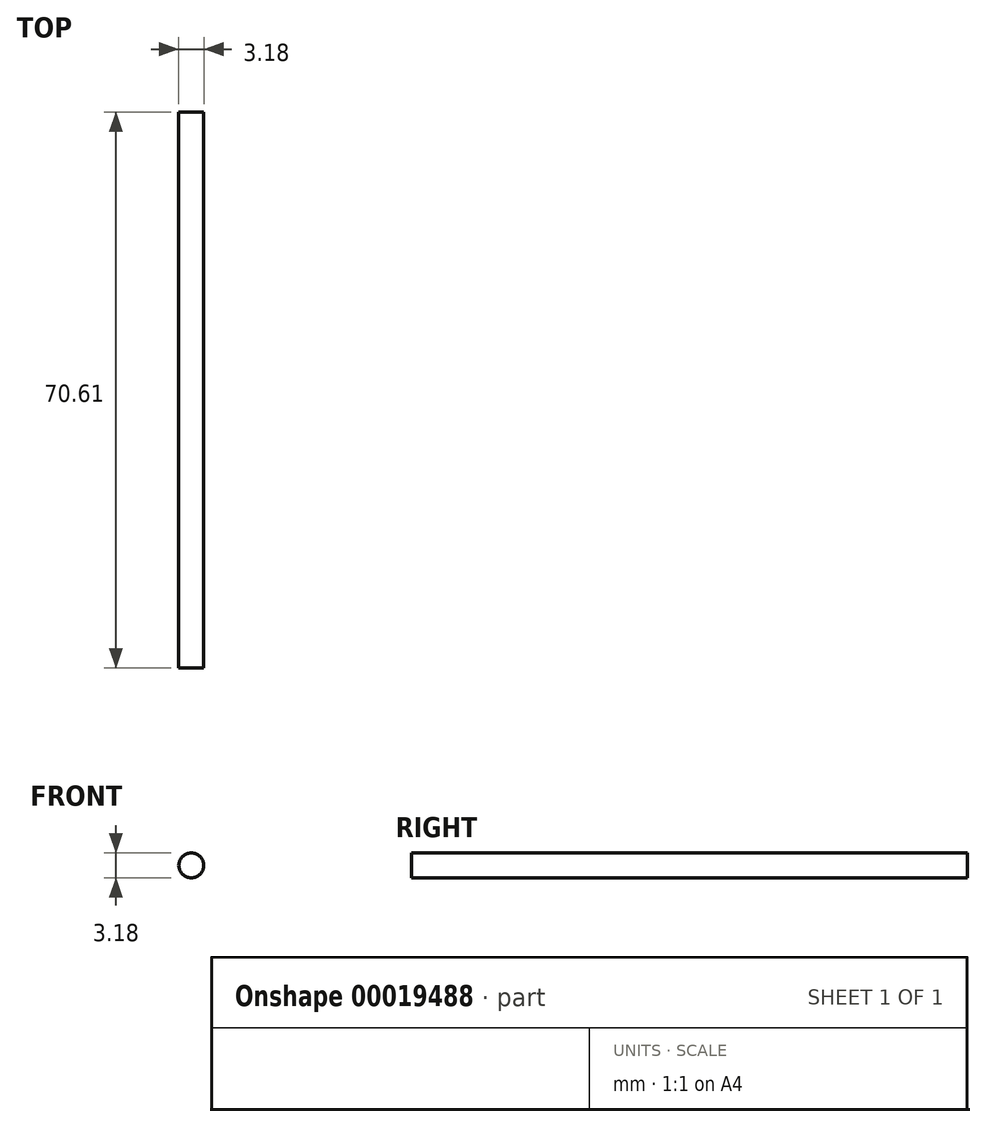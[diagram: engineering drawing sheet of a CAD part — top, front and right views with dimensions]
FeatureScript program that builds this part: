
annotation { "Feature Type Name" : "Feature", "Feature Type Description" : "" }
export const myFeature = defineFeature(function(context is Context, id is Id, definition is map)
    precondition{}
    {
        {
            var Q0;
            Q0=qCreatedBy(makeId("Front.planeOp"),FACE);
            var sketch = newSketch(context, id + "F0", { "sketchPlane" : qUnion([Q0])});
            skCircle(sketch, "E0", {"center": v(0, 0) * mm, "radius": 1.59 * mm});
            skSolve(sketch);
        }
        {
            var Q0;
            Q0 = qSketchRegion(id + "F0", true);
            extrude(context, id + "F1", {"entities" : qUnion([Q0]), "depth" : 70.61 * mm});
        }
    });
